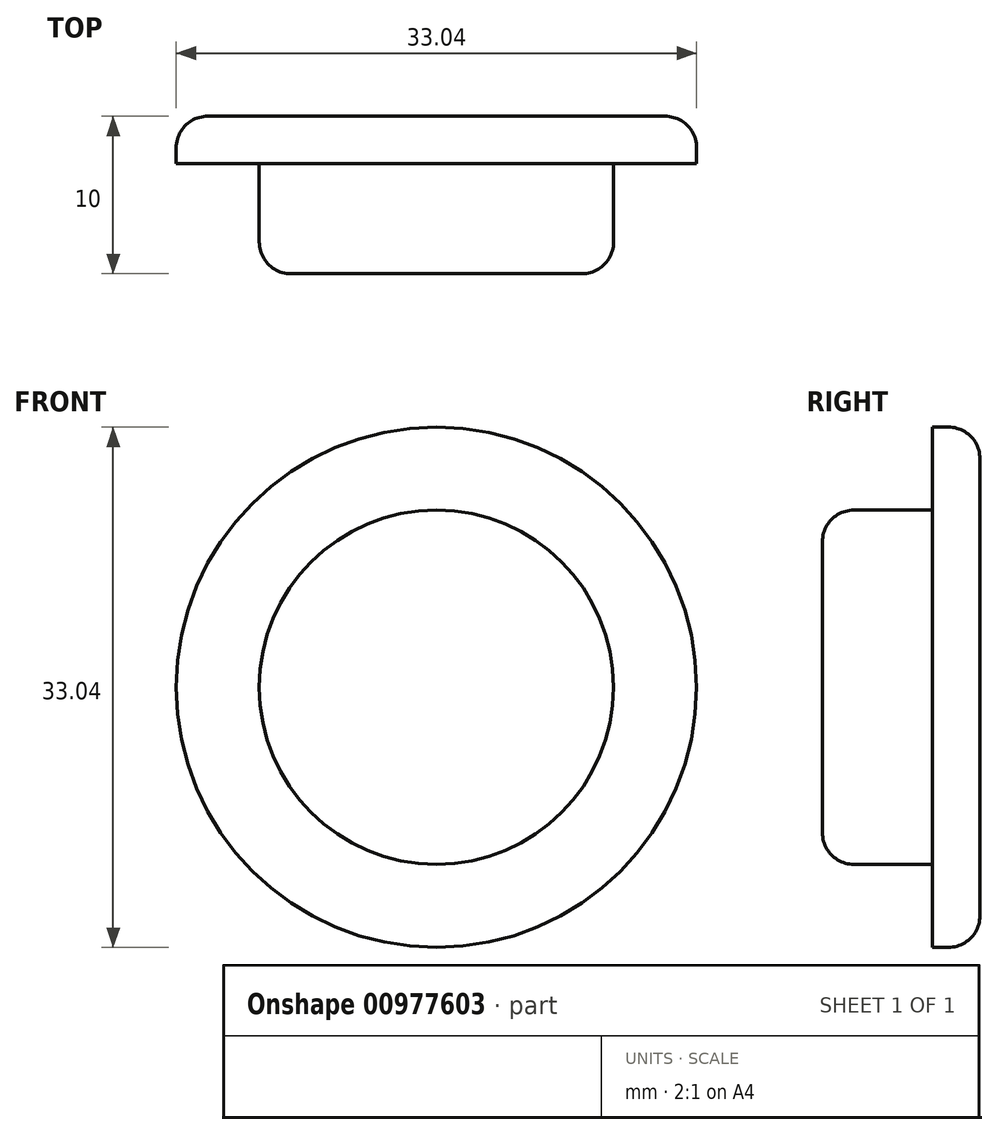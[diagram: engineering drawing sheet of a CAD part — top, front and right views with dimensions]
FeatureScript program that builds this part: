
annotation { "Feature Type Name" : "Feature", "Feature Type Description" : "" }
export const myFeature = defineFeature(function(context is Context, id is Id, definition is map)
    precondition{}
    {
        {
            var Q0;
            Q0=qCreatedBy(makeId("Front.planeOp"),FACE);
            var sketch = newSketch(context, id + "F0", { "sketchPlane" : qUnion([Q0])});
            skCircle(sketch, "E0", {"center": v(0, 0) * mm, "radius": 11.25 * mm});
            skCircle(sketch, "E1", {"center": v(0, 0) * mm, "radius": 16.52 * mm});
            skSolve(sketch);
        }
        {
            var Q0;
            Q0 = qSketchRegion(id + "F0", true);
            extrude(context, id + "F1", {"entities" : qUnion([Q0]), "depth" : 3 * mm, "offsetDistance" : 25 * mm});
        }
        {
            var Q0;
            Q0=makeQuery(id+"F0.imprint","IMPRINT",FACE,{"disambiguationData":[TD([[makeQuery(id+"F0.imprint","IMPRINT",EDGE,{"derivedFrom":sQuery(id+"F0.wireOp",EDGE,"E0")}),1.0]])]});
            extrude(context, id + "F2", {"entities" : qUnion([Q0]), "operationType" : NewBodyOperationType.ADD, "depth" : 10 * mm, "offsetDistance" : 25 * mm});
        }
        {
            var Q0;
            Q0=makeQuery(id+"F1.opExtrude","CAP_EDGE",EDGE,{"disambiguationData":[OSD([sQuery(id+"F0.wireOp",EDGE,"E1")])],"isStart":true});
            fillet(context, id + "F3", {"entities" : qUnion([Q0]), "radius" : 2 * mm, "tangentPropagation" : true, "allowEdgeOverflow" : false});
        }
        {
            var Q0;
            Q0=makeQuery(id+"F2.opExtrude","CAP_EDGE",EDGE,{"disambiguationData":[OSD([sQuery(id+"F0.wireOp",EDGE,"E0")])],"isStart":false});
            fillet(context, id + "F4", {"entities" : qUnion([Q0]), "radius" : 2 * mm, "tangentPropagation" : true, "allowEdgeOverflow" : false});
        }
    });
